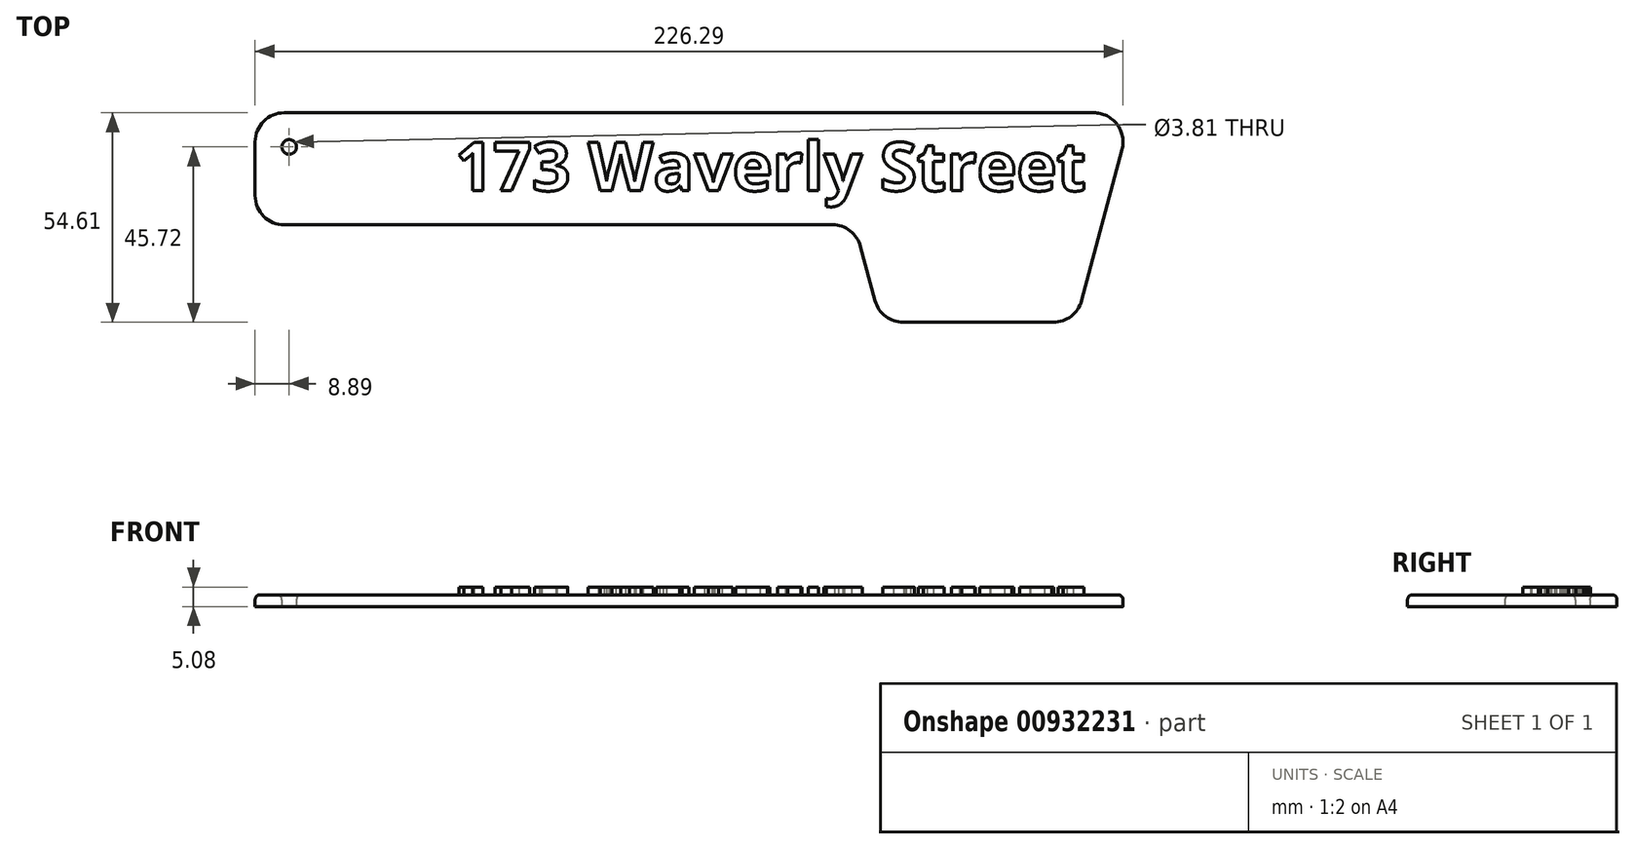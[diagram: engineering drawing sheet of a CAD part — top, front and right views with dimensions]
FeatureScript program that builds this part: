
annotation { "Feature Type Name" : "Feature", "Feature Type Description" : "" }
export const myFeature = defineFeature(function(context is Context, id is Id, definition is map)
    precondition{}
    {
        {
            var Q0;
            Q0=qCreatedBy(makeId("Top.planeOp"),FACE);
            var sketch = newSketch(context, id + "F0", { "sketchPlane" : qUnion([Q0])});
            skCircle(sketch, "E0", {"center": v(0, 0) * mm, "radius": 1.9 * mm});
            skLineSegment(sketch, "E1.bottom", {"start": v(-8.9, 8.9) * mm, "end": v(219.71, 8.9) * mm});
            skLineSegment(sketch, "E1.top", {"start": v(-8.89, -20.32) * mm, "end": v(147.47, -20.32) * mm});
            skLineSegment(sketch, "E1.left", {"start": v(-8.9, 8.9) * mm, "end": v(-8.89, -20.32) * mm});
            skLineSegment(sketch, "E2", {"start": v(147.47, -20.32) * mm, "end": v(154.28, -45.72) * mm});
            skLineSegment(sketch, "E3", {"start": v(154.28, -45.72) * mm, "end": v(205.08, -45.72) * mm});
            skLineSegment(sketch, "E4", {"start": v(205.08, -45.72) * mm, "end": v(219.71, 8.9) * mm});
            skSolve(sketch);
        }
        {
            var Q0;
            Q0=makeQuery(id+"F0.imprint","IMPRINT",FACE,{"disambiguationData":[TD([[makeQuery(id+"F0.imprint","IMPRINT",EDGE,{"derivedFrom":sQuery(id+"F0.wireOp",EDGE,"E0")}),-1.0]])]});
            extrude(context, id + "F1", {"entities" : qUnion([Q0]), "depth" : 3.05 * mm, "offsetDistance" : 25.4 * mm});
        }
        {
            var Q0;
            Q0=makeQuery(id+"F1.opExtrude","SWEPT_EDGE",EDGE,{"disambiguationData":[OSD([sQuery(id+"F0.wireOp",EDGE,"E2"),sQuery(id+"F0.wireOp",EDGE,"E3")])]});
            var Q1;
            Q1=makeQuery(id+"F1.opExtrude","SWEPT_EDGE",EDGE,{"disambiguationData":[OSD([sQuery(id+"F0.wireOp",EDGE,"E3"),sQuery(id+"F0.wireOp",EDGE,"E4")])]});
            var Q2;
            Q2=makeQuery(id+"F1.opExtrude","SWEPT_EDGE",EDGE,{"disambiguationData":[OSD([sQuery(id+"F0.wireOp",EDGE,"E1.bottom"),sQuery(id+"F0.wireOp",EDGE,"E4")])]});
            var Q3;
            Q3=makeQuery(id+"F1.opExtrude","SWEPT_EDGE",EDGE,{"disambiguationData":[OSD([sQuery(id+"F0.wireOp",EDGE,"E1.top"),sQuery(id+"F0.wireOp",EDGE,"E1.left")])]});
            var Q4;
            Q4=makeQuery(id+"F1.opExtrude","SWEPT_EDGE",EDGE,{"disambiguationData":[OSD([sQuery(id+"F0.wireOp",EDGE,"E1.bottom"),sQuery(id+"F0.wireOp",EDGE,"E1.left")])]});
            var Q5;
            Q5=makeQuery(id+"F1.opExtrude","SWEPT_EDGE",EDGE,{"disambiguationData":[OSD([sQuery(id+"F0.wireOp",EDGE,"E1.top"),sQuery(id+"F0.wireOp",EDGE,"E2")])]});
            fillet(context, id + "F2", {"entities" : qUnion([Q0, Q1, Q2, Q3, Q4, Q5]), "radius" : 7.62 * mm, "tangentPropagation" : true, "allowEdgeOverflow" : false});
        }
        {
            var Q0;
            Q0=makeQuery(id+"F1.opExtrude","CAP_FACE",FACE,{"disambiguationData":[OSD([sQuery(id+"F0.wireOp",EDGE,"E0"),sQuery(id+"F0.wireOp",EDGE,"E1.bottom"),sQuery(id+"F0.wireOp",EDGE,"E1.top"),sQuery(id+"F0.wireOp",EDGE,"E1.left"),sQuery(id+"F0.wireOp",EDGE,"E2"),sQuery(id+"F0.wireOp",EDGE,"E3"),sQuery(id+"F0.wireOp",EDGE,"E4")])],"isStart":false});
            fillet(context, id + "F3", {"entities" : qUnion([Q0]), "radius" : 1.27 * mm, "tangentPropagation" : true, "allowEdgeOverflow" : false});
        }
        {
            var Q0;
            Q0=makeQuery(id+"F1.opExtrude","CAP_FACE",FACE,{"disambiguationData":[OSD([sQuery(id+"F0.wireOp",EDGE,"E0"),sQuery(id+"F0.wireOp",EDGE,"E1.bottom"),sQuery(id+"F0.wireOp",EDGE,"E1.top"),sQuery(id+"F0.wireOp",EDGE,"E1.left"),sQuery(id+"F0.wireOp",EDGE,"E2"),sQuery(id+"F0.wireOp",EDGE,"E3"),sQuery(id+"F0.wireOp",EDGE,"E4")])],"isStart":false});
            var sketch = newSketch(context, id + "F4", { "sketchPlane" : qUnion([Q0])});
            skText(sketch, "E5", { "text": "173 Waverly Street", "fontName": "OpenSans-Bold.ttf"});
            const initialGuessF4  = {"E5": [0.04318, -0.01143, 1, 0, 0.01268]};
            skSetInitialGuess(sketch, initialGuessF4);
            skSolve(sketch);
        }
        {
            var Q0;
            Q0 = qSketchRegion(id + "F4", true);
            extrude(context, id + "F5", {"entities" : qUnion([Q0]), "operationType" : NewBodyOperationType.ADD, "depth" : 2.03 * mm, "offsetDistance" : 25.4 * mm});
        }
    });
